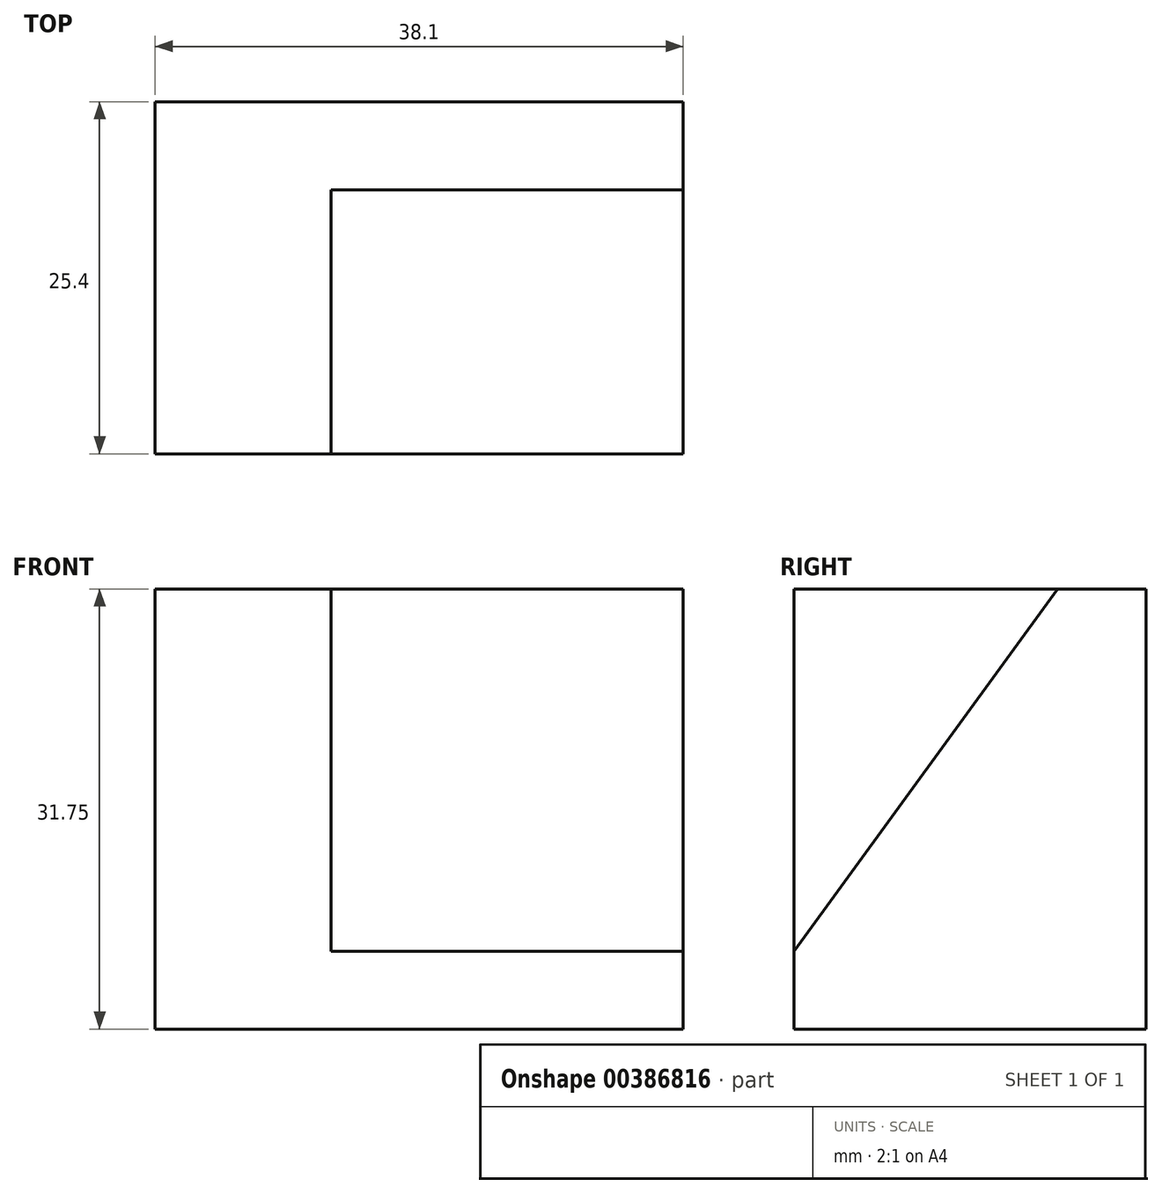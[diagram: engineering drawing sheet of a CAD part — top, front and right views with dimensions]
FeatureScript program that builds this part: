
annotation { "Feature Type Name" : "Feature", "Feature Type Description" : "" }
export const myFeature = defineFeature(function(context is Context, id is Id, definition is map)
    precondition{}
    {
        {
            var Q0;
            Q0=qCreatedBy(makeId("Top.planeOp"),FACE);
            var sketch = newSketch(context, id + "F0", { "sketchPlane" : qUnion([Q0])});
            skLineSegment(sketch, "E0", {"start": v(-35.44, 25.4) * mm, "end": v(2.66, 25.4) * mm});
            skLineSegment(sketch, "E1", {"start": v(2.66, 25.4) * mm, "end": v(2.66, 0) * mm});
            skLineSegment(sketch, "E2", {"start": v(2.66, 0) * mm, "end": v(-35.44, 0) * mm});
            skLineSegment(sketch, "E3", {"start": v(-35.44, 0) * mm, "end": v(-35.44, 25.4) * mm});
            skSolve(sketch);
        }
        {
            var Q0;
            Q0=makeQuery(id+"F0.imprint","IMPRINT",FACE,{"disambiguationData":[TD([[makeQuery(id+"F0.imprint","IMPRINT",EDGE,{"derivedFrom":sQuery(id+"F0.wireOp",EDGE,"E0")}),-1.0]])]});
            extrude(context, id + "F1", {"entities" : qUnion([Q0]), "depth" : 31.75 * mm});
        }
        {
            var Q0;
            Q0=makeQuery(id+"F1.opExtrude","SWEPT_FACE",FACE,{"disambiguationData":[OSD([sQuery(id+"F0.wireOp",EDGE,"E2")])]});
            var sketch = newSketch(context, id + "F2", { "sketchPlane" : qUnion([Q0])});
            skSolve(sketch);
        }
        {
            var Q0;
            Q0=makeQuery(id+"F1.opExtrude","SWEPT_FACE",FACE,{"disambiguationData":[OSD([sQuery(id+"F0.wireOp",EDGE,"E1")])]});
            var sketch = newSketch(context, id + "F3", { "sketchPlane" : qUnion([Q0])});
            skLineSegment(sketch, "E4", {"start": v(0, 5.6) * mm, "end": v(19.02, 31.75) * mm});
            skSolve(sketch);
        }
        {
            var Q0;
            {var subQ0=sQuery(id+"F3.wireOp",EDGE,"E4");Q0=makeQuery(id+"F3.imprint","IMPRINT",FACE,{"disambiguationData":[TD([[makeQuery(id+"F3.imprint","IMPRINT",EDGE,{"derivedFrom":subQ0}),1.0]])]});}
            extrude(context, id + "F4", {"entities" : qUnion([Q0]), "operationType" : NewBodyOperationType.REMOVE, "oppositeDirection" : true, "depth" : 25.4 * mm});
        }
    });
